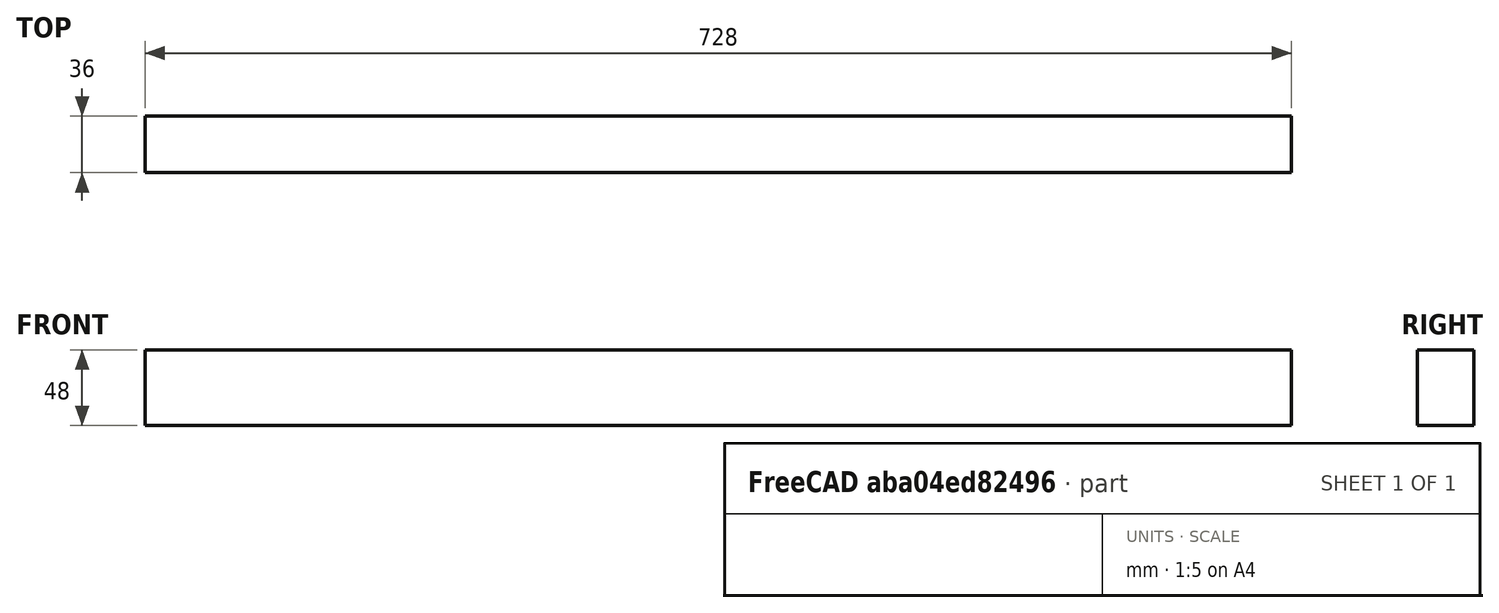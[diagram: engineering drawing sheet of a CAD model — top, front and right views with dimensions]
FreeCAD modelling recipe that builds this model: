
FCSTD DOCUMENT  (FreeCAD 0.19R24267 (Git))
Label: windowFrameWidth
License: Creative Commons Attribution-ShareAlike
LicenseURL: http://creativecommons.org/licenses/by-sa/4.0/
objects: Sketcher::SketchObject×1, Part::Extrusion×1
note: 2 computed .brp shape members not serialized (recipe doc carries the construction recipe); baked Part::Feature solids carry a one-line shape summary decoded from their .brp
EXTERNAL_REF file=Main.FCStd obj=Spreadsheet

FEATURE [Sketcher::SketchObject] Sketch
  FullyConstrained = true
  expr: Constraints[9] = Main#<<params>>.outerWidth - Main#<<params>>.structuralWoodHeight * 2
  expr: Constraints[8] = Main#<<params>>.structuralWoodHeight
  sketch-geometry (4):
    g0: LineSegment StartX=0 StartY=0 StartZ=0 EndX=2.2e-15 EndY=36 EndZ=0
    g1: LineSegment StartX=2.2e-15 StartY=36 StartZ=0 EndX=728 EndY=36 EndZ=0
    g2: LineSegment StartX=728 StartY=36 StartZ=0 EndX=728 EndY=0 EndZ=0
    g3: LineSegment StartX=728 StartY=0 StartZ=0 EndX=0 EndY=0 EndZ=0
  constraints (11):
    c: Coincident(g-1,g0)
    c: Coincident(g0,g1)
    c: Horizontal(g1)
    c: Coincident(g1,g2)
    c: PointOnObject(g2,g-1)
    c: Coincident(g2,g3)
    c: Coincident(g3,g0)
    c: Angle(g3,g0) = 1.5708
    c: DistanceY(g0,g0) = 36
    c: Distance(g3) = 728
    c: Equal(g0,g2)
FEATURE [Part::Extrusion] Extrude
  Base = -> Sketch
  Dir = (0,0,1)
  DirMode = 2
  FaceMakerClass = Part::FaceMakerBullseye
  LengthFwd = 48
  LengthRev = 0
  Solid = true
  Symmetric = false
  expr: LengthFwd = Main#<<params>>.structuralWoodWidth
